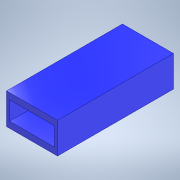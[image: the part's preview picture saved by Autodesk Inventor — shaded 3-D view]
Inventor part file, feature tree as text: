
AUTODESK INVENTOR PART (.ipt)
format: ipt  version: 2022 (Build 260153000, 153)  size: 101,376 bytes
history: native  units: mm
features: extrude x1, sketch x1
ambient origin geometry x8: Origin, YZ Plane, XZ Plane, XY Plane, X Axis, Y Axis, Z Axis, Center Point
bodies: Solid1 (feature_tree)
feature tree (2):
  extrude  "Extrusion1"  Depth=12.0mm
  sketch  "Sketch1"  dims[d0=4.0mm d1=12.0mm d2=29.0mm d3=75.0mm d4=0.0mm d5=2.0mm d6=2.0mm]
